# Revit family: Контроллер второго уровня PERCo_CL211.3, CL211.9
name_source: partatom
category: Охранная сигнализация
units: mm (PartAtom-declared; Revit-internal decimal feet)

## family parameters
Общий = Нет
Основа = Грань
При загрузке вырезать с полостями = Нет
Размер круглого соединителя = Использовать диаметр
Сохранять ориентацию аннотаций = Да
Тип детали = Нормальный
Точка расчета площади = Нет

## types (2) — shared parameters
ADSK_URL страницы изделия = https://www.perco.ru
ADSK_Единица измерения = шт.
ADSK_Завод-изготовитель = PERCo
ADSK_Количество = 1
ADSK_Масса_Текст = не более 0,3 кг
ADSK_Материал наименование = Корпус выполнен из ударопрочного АБС-пластика
ADSK_Напряжение = 12 В
ADSK_Номинальная мощность = 2 В·А
ADSK_Ток = 0 А
Габаритные размеры = 150×50×20 мм
Кол-во выносных считывателей = Не предусмотрено
Кол-во контроллеров 2-го уровня = Не предусмотрено
Кол-во подключаемых замков = 1
Кол-во подключаемых турникетов = Не предусмотрено
Кол-во пользователей = до 50 000
Кол-во событий = Не предусмотрено
Наличие встроенного считывателя = Да
Наличие сканера отпечатка пальцев = Нет
Отметка по умолчанию = 1500 мм
Подключение к электросети = 220В
Степень защиты оболочки = IP54
Температура использования = от -40°C до +45°C
Тип интерфейса = RS-485

## per-type parameters (varying)
| type | ADSK_Наименование | ADSK_Наименование краткое | Формат читаемых карт |
| CL211.3 | Контроллер PERCo-CL211.3 со встроенным считывателем для карт формата EMM/HID | Контроллер CL211.3 | EMM, HID Prox |
| CL211.9 | Контроллер PERCo-CL211.9 со встроенным считывателем для карт формата EMM/HID/Mifare | Контроллер CL211.9 | Mifare, EMM, HID Prox |
